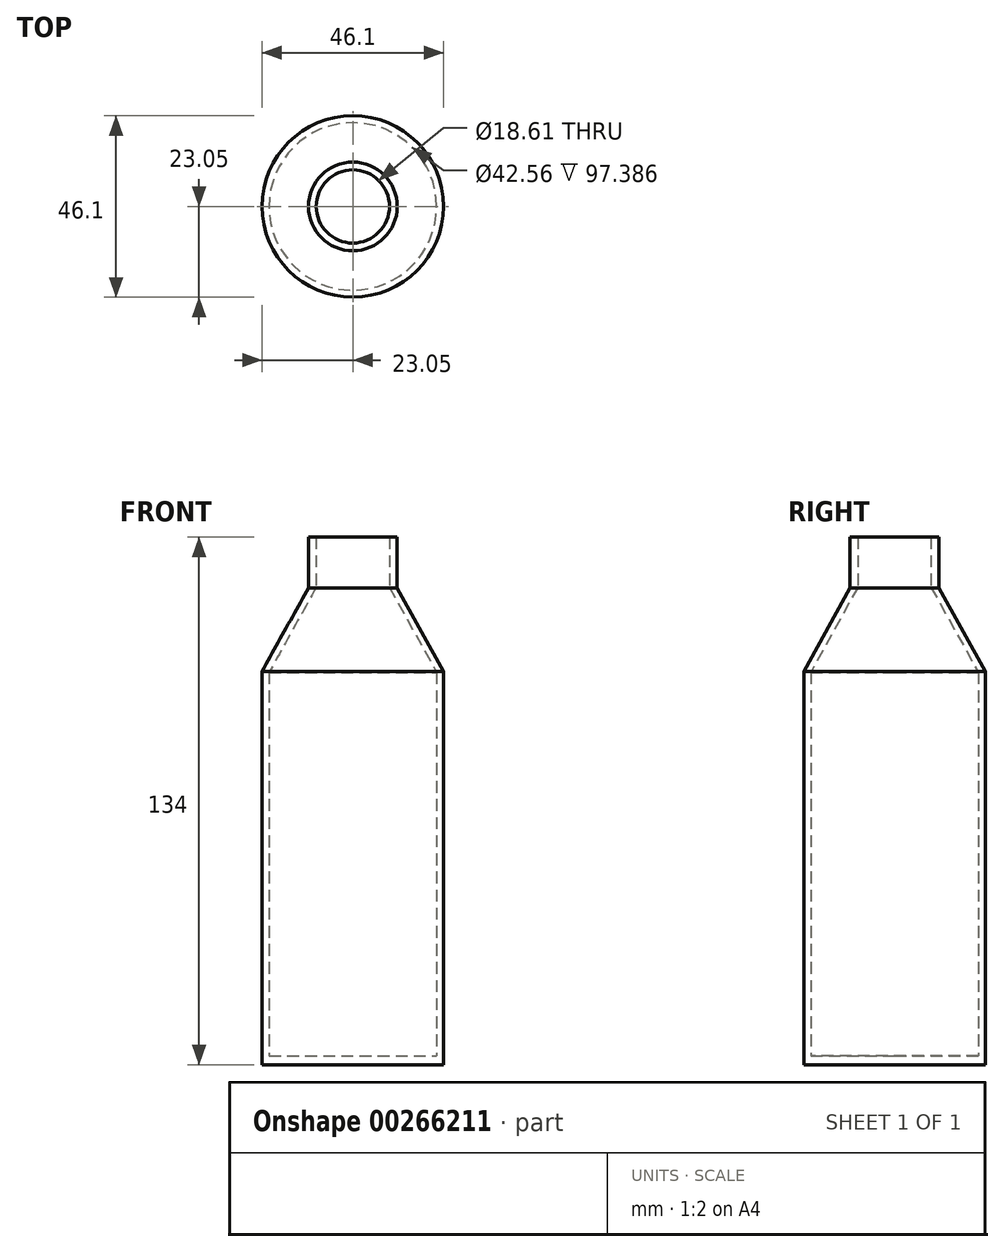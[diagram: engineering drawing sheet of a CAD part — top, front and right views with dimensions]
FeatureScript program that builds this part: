
annotation { "Feature Type Name" : "Feature", "Feature Type Description" : "" }
export const myFeature = defineFeature(function(context is Context, id is Id, definition is map)
    precondition{}
    {
        {
            var Q0;
            Q0=qCreatedBy(makeId("Front.planeOp"),FACE);
            var sketch = newSketch(context, id + "F0", { "sketchPlane" : qUnion([Q0])});
            skLineSegment(sketch, "E0", {"start": v(0, -75.4) * mm, "end": v(23.05, -75.4) * mm});
            skLineSegment(sketch, "E1", {"start": v(23.05, -75.4) * mm, "end": v(23.05, 24.52) * mm});
            skLineSegment(sketch, "E2", {"start": v(23.05, 24.52) * mm, "end": v(15.5, 38.16) * mm});
            skLineSegment(sketch, "E3", {"start": v(15.5, 38.16) * mm, "end": v(11.28, 45.76) * mm});
            skLineSegment(sketch, "E4", {"start": v(11.28, 45.76) * mm, "end": v(11.28, 58.6) * mm});
            skLineSegment(sketch, "E5", {"start": v(9.3, 58.6) * mm, "end": v(9.3, 45.87) * mm});
            skLineSegment(sketch, "E6", {"start": v(9.3, 45.87) * mm, "end": v(21.28, 24.26) * mm});
            skLineSegment(sketch, "E7", {"start": v(21.28, 24.26) * mm, "end": v(21.28, -73.13) * mm});
            skLineSegment(sketch, "E8", {"start": v(21.28, -73.13) * mm, "end": v(0, -73.13) * mm});
            skLineSegment(sketch, "E9", {"start": v(11.28, 58.6) * mm, "end": v(9.3, 58.6) * mm});
            skLineSegment(sketch, "E10", {"start": v(9.3, 58.6) * mm, "end": v(11.28, 58.6) * mm});
            skLineSegment(sketch, "E11", {"start": v(0, -75.4) * mm, "end": v(0, -73.13) * mm});
            skSolve(sketch);
        }
        {
            var Q0;
            Q0 = qSketchRegion(id + "F0", true);
            var Q1;
            Q1=sQuery(id+"F0.wireOp",EDGE,"E11");
            revolve(context, id + "F1", {"entities" : qUnion([Q0]), "axis" : qUnion([Q1]), "revolveType" : RevolveType.FULL});
        }
    });
